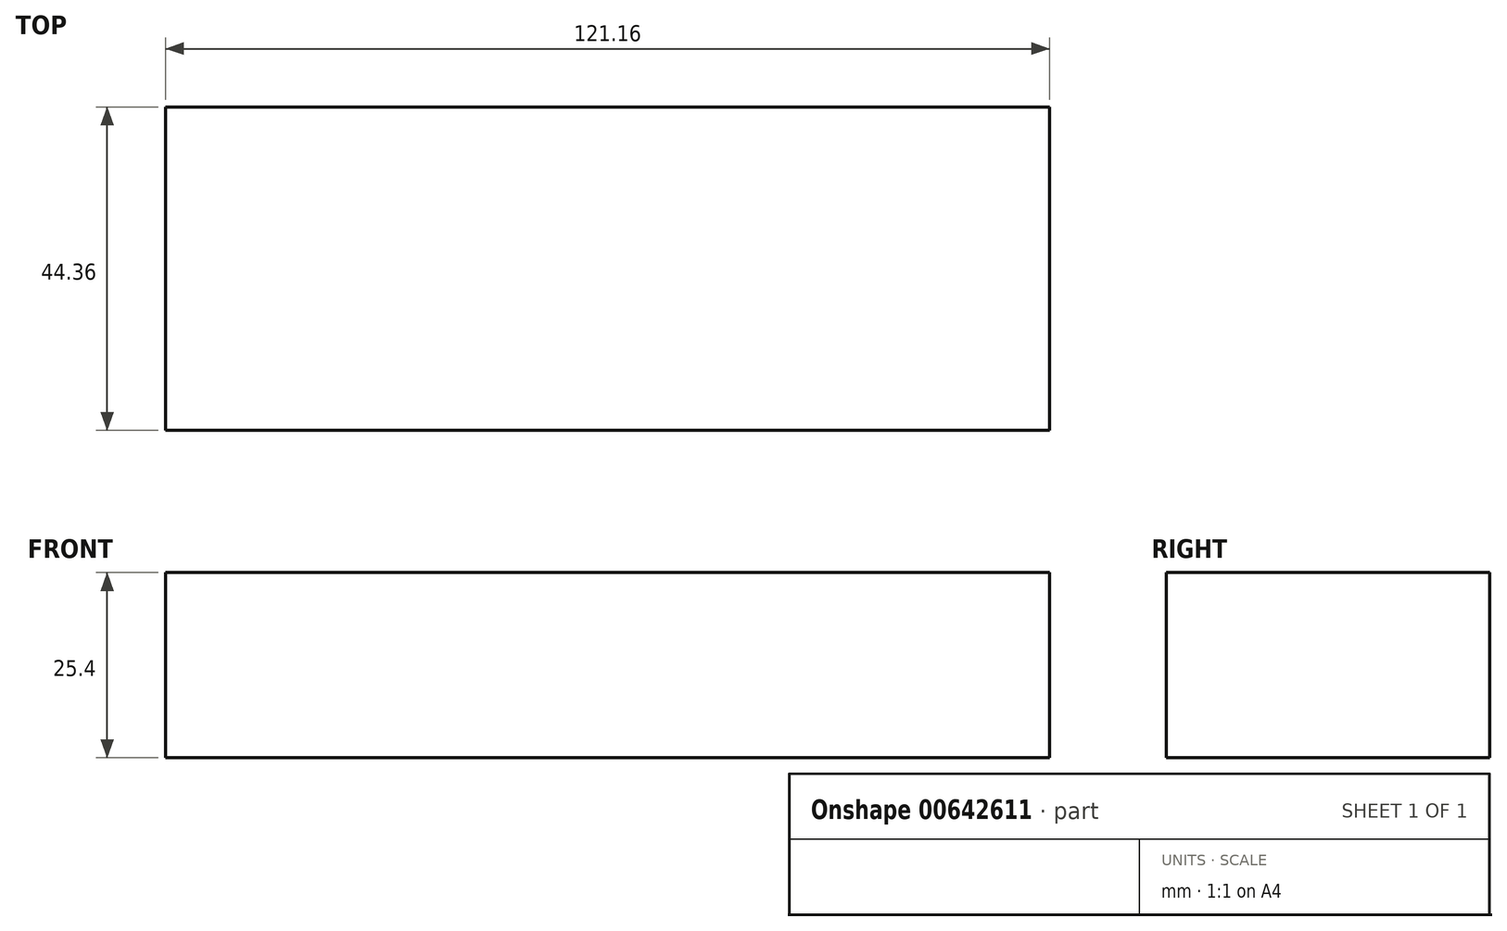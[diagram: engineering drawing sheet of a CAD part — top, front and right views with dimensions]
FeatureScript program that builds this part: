
annotation { "Feature Type Name" : "Feature", "Feature Type Description" : "" }
export const myFeature = defineFeature(function(context is Context, id is Id, definition is map)
    precondition{}
    {
        {
            var Q0;
            Q0=qCreatedBy(makeId("Top.planeOp"),FACE);
            var sketch = newSketch(context, id + "F0", { "sketchPlane" : qUnion([Q0])});
            skLineSegment(sketch, "E0.bottom", {"start": v(0, 0) * mm, "end": v(121.16, 0) * mm});
            skLineSegment(sketch, "E0.top", {"start": v(0, -44.36) * mm, "end": v(121.16, -44.36) * mm});
            skLineSegment(sketch, "E0.left", {"start": v(0, 0) * mm, "end": v(0, -44.36) * mm});
            skLineSegment(sketch, "E0.right", {"start": v(121.16, 0) * mm, "end": v(121.16, -44.36) * mm});
            skSolve(sketch);
        }
        {
            var Q0;
            Q0=makeQuery(id+"F0.imprint","IMPRINT",FACE,{"disambiguationData":[TD([[makeQuery(id+"F0.imprint","IMPRINT",EDGE,{"derivedFrom":sQuery(id+"F0.wireOp",EDGE,"E0.bottom")}),-1.0]])]});
            extrude(context, id + "F1", {"entities" : qUnion([Q0]), "depth" : 25.4 * mm, "offsetDistance" : 25.4 * mm});
        }
    });
